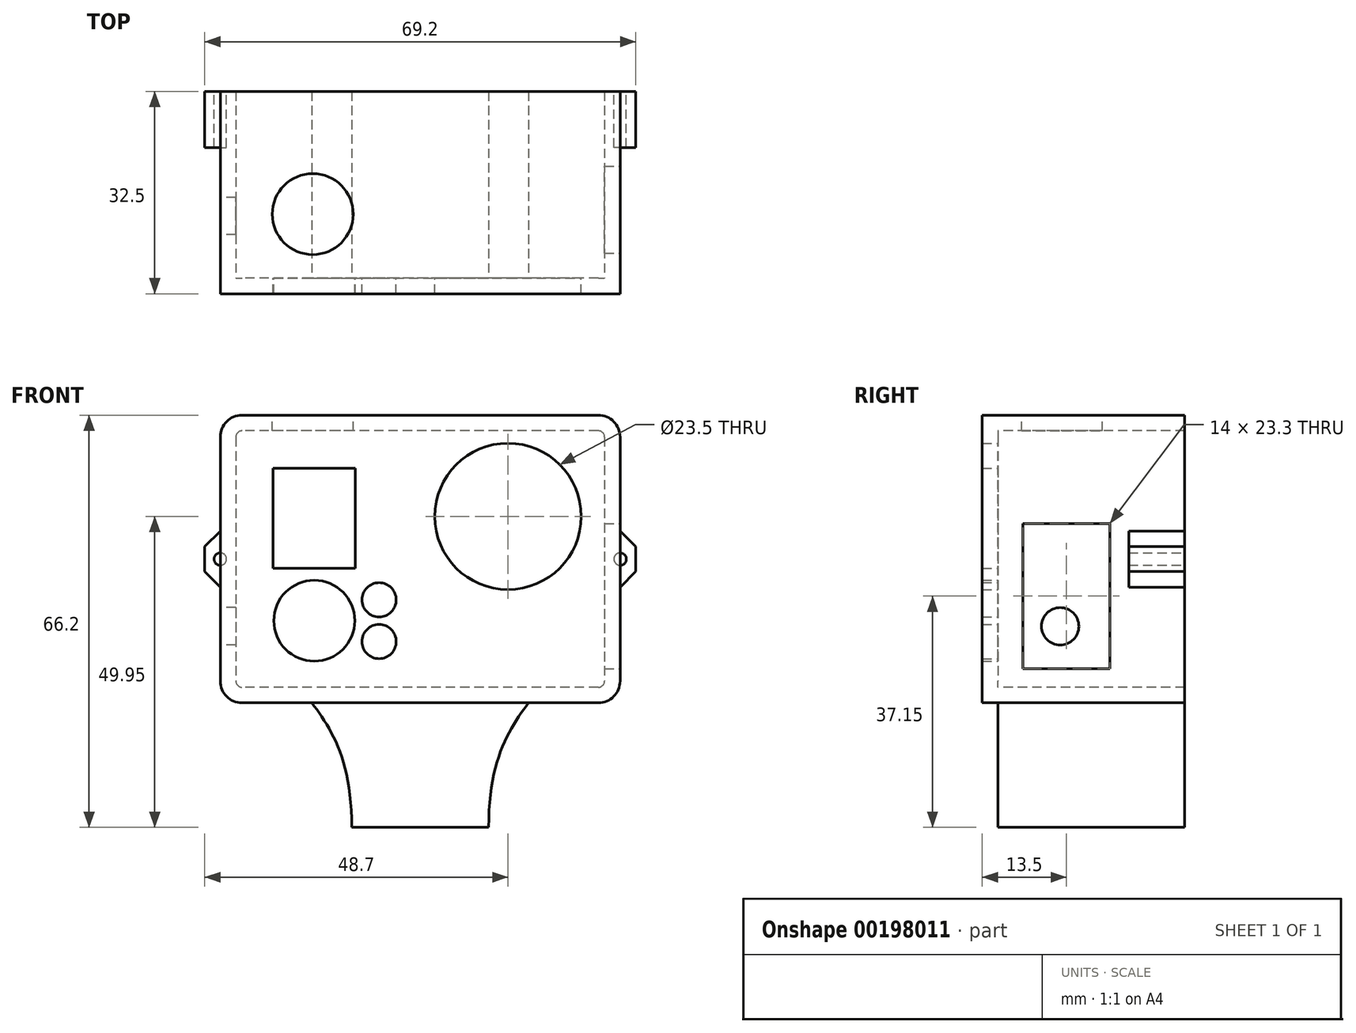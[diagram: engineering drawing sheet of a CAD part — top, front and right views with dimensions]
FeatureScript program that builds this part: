
annotation { "Feature Type Name" : "Feature", "Feature Type Description" : "" }
export const myFeature = defineFeature(function(context is Context, id is Id, definition is map)
    precondition{}
    {
        {
            var Q0;
            Q0=qCreatedBy(makeId("Front.planeOp"),FACE);
            var sketch = newSketch(context, id + "F0", { "sketchPlane" : qUnion([Q0])});
            skLineSegment(sketch, "E0.bottom", {"start": v(28.6, 20.6) * mm, "end": v(-28.6, 20.6) * mm});
            skLineSegment(sketch, "E0.top", {"start": v(28.6, -20.6) * mm, "end": v(-28.6, -20.6) * mm});
            skLineSegment(sketch, "E0.left", {"start": v(29.6, 19.6) * mm, "end": v(29.6, -19.6) * mm});
            skLineSegment(sketch, "E0.right", {"start": v(-29.6, 19.6) * mm, "end": v(-29.6, -19.6) * mm});
            skPoint(sketch, "E0.middle", {"position": v(0, 0) * mm});
            skCircle(sketch, "E1", {"center": v(14.1, 6.85) * mm, "radius": 11.75 * mm});
            skLineSegment(sketch, "E2.bottom", {"start": v(-23.6, 14.6) * mm, "end": v(-10.4, 14.6) * mm});
            skLineSegment(sketch, "E2.top", {"start": v(-23.6, -1.5) * mm, "end": v(-10.4, -1.5) * mm});
            skLineSegment(sketch, "E2.left", {"start": v(-23.6, 14.6) * mm, "end": v(-23.6, -1.5) * mm});
            skLineSegment(sketch, "E2.right", {"start": v(-10.4, 14.6) * mm, "end": v(-10.4, -1.5) * mm});
            skCircle(sketch, "E3", {"center": v(-17, -9.9) * mm, "radius": 6.5 * mm});
            skPoint(sketch, "E4", {"position": v(-17, -1.5) * mm});
            skCircle(sketch, "E5", {"center": v(-6.6, -13.25) * mm, "radius": 2.75 * mm});
            skLineSegment(sketch, "E6", {"start": v(-17, -9.9) * mm, "end": v(4.32, -9.9) * mm, "construction": true});
            skCircle(sketch, "E7.MirrorC", {"center": v(-6.6, -6.55) * mm, "radius": 2.75 * mm});
            skPoint(sketch, "E8.visualSharp", {"position": v(-29.6, 20.6) * mm});
            skArc(sketch, "E8.filletArc", {"start": v(-28.6, 20.6) * mm, "mid": v(-29.3, 20.3) * mm, "end": v(-29.6, 19.6) * mm});
            skPoint(sketch, "E9.visualSharp", {"position": v(-29.6, -20.6) * mm});
            skArc(sketch, "E9.filletArc", {"start": v(-29.6, -19.6) * mm, "mid": v(-29.3, -20.3) * mm, "end": v(-28.6, -20.6) * mm});
            skPoint(sketch, "E10.visualSharp", {"position": v(29.6, -20.6) * mm});
            skArc(sketch, "E10.filletArc", {"start": v(28.6, -20.6) * mm, "mid": v(29.3, -20.3) * mm, "end": v(29.6, -19.6) * mm});
            skPoint(sketch, "E11.visualSharp", {"position": v(29.6, 20.6) * mm});
            skArc(sketch, "E11.filletArc", {"start": v(29.6, 19.6) * mm, "mid": v(29.3, 20.3) * mm, "end": v(28.6, 20.6) * mm});
            skArc(sketch, "E12.0", {"start": v(32.1, 19.6) * mm, "mid": v(31.07, 22.07) * mm, "end": v(28.6, 23.1) * mm});
            skLineSegment(sketch, "E12.1", {"start": v(32.1, 19.6) * mm, "end": v(32.1, -19.6) * mm});
            skLineSegment(sketch, "E12.2", {"start": v(28.6, 23.1) * mm, "end": v(-28.6, 23.1) * mm});
            skArc(sketch, "E12.3", {"start": v(28.6, -23.1) * mm, "mid": v(31.07, -22.07) * mm, "end": v(32.1, -19.6) * mm});
            skArc(sketch, "E12.4", {"start": v(-28.6, 23.1) * mm, "mid": v(-31.07, 22.07) * mm, "end": v(-32.1, 19.6) * mm});
            skLineSegment(sketch, "E12.5", {"start": v(-32.1, 19.6) * mm, "end": v(-32.1, -19.6) * mm});
            skArc(sketch, "E12.6", {"start": v(-32.1, -19.6) * mm, "mid": v(-31.07, -22.07) * mm, "end": v(-28.6, -23.1) * mm});
            skLineSegment(sketch, "E12.7", {"start": v(28.6, -23.1) * mm, "end": v(-28.6, -23.1) * mm});
            skLineSegment(sketch, "E13", {"start": v(-11, -43.1) * mm, "end": v(11, -43.1) * mm});
            skPoint(sketch, "E14", {"position": v(0, -23.1) * mm});
            skPoint(sketch, "E15", {"position": v(0, -43.1) * mm});
            skLineSegment(sketch, "E16", {"start": v(-22.15, -12.1) * mm, "end": v(22.15, -12.1) * mm, "construction": true});
            skPoint(sketch, "E17", {"position": v(0, -12.1) * mm});
            skFitSpline(sketch, "E18", {"points": [v(22.15, -12.1) * mm, v(11, -43.1) * mm], "startDerivative": vector(0, -33) * mm, "endDerivative": vector(0, -60) * mm});
            skFitSpline(sketch, "E19", {"points": [v(-22.15, -12.1) * mm, v(-11, -43.1) * mm], "startDerivative": vector(0, -33) * mm, "endDerivative": vector(0, -60) * mm});
            skLineSegment(sketch, "E20", {"start": v(-24.4, -45.93) * mm, "end": v(17.2, -45.93) * mm, "construction": true});
            skSolve(sketch);
        }
        {
            var Q0;
            Q0=makeQuery(id+"F0.imprint","IMPRINT",FACE,{"disambiguationData":[TD([[makeQuery(id+"F0.imprint","IMPRINT",EDGE,{"derivedFrom":sQuery(id+"F0.wireOp",EDGE,"E0.bottom")}),-1.0]])]});
            var Q1;
            {var subQ0=sQuery(id+"F0.wireOp",EDGE,"E18");var subQ1=sQuery(id+"F0.wireOp",EDGE,"E0.top");var subQ2=makeQuery(id+"F0.imprint","INTERSECT",VERTEX,{"derivedFrom":[subQ1,subQ0]});Q1=makeQuery(id+"F0.imprint","IMPRINT",FACE,{"disambiguationData":[TD([[makeQuery(id+"F0.imprint","IMPRINT",EDGE,{"disambiguationData":[TD([[subQ2,-1.0]])],"derivedFrom":subQ1}),1.0]])]});}
            var Q2;
            {var subQ5=sQuery(id+"F0.wireOp",EDGE,"E13");Q2=makeQuery(id+"F0.imprint","IMPRINT",FACE,{"disambiguationData":[TD([[makeQuery(id+"F0.imprint","IMPRINT",EDGE,{"derivedFrom":subQ5}),1.0]])]});}
            extrude(context, id + "F1", {"entities" : qUnion([Q0, Q1, Q2]), "oppositeDirection" : true, "depth" : 30 * mm});
        }
        {
            var Q0;
            Q0=makeQuery(id+"F0.imprint","IMPRINT",FACE,{"disambiguationData":[TD([[makeQuery(id+"F0.imprint","IMPRINT",EDGE,{"derivedFrom":sQuery(id+"F0.wireOp",EDGE,"E0.bottom")}),-1.0]])]});
            var Q1;
            Q1=makeQuery(id+"F0.imprint","IMPRINT",FACE,{"disambiguationData":[TD([[makeQuery(id+"F0.imprint","IMPRINT",EDGE,{"derivedFrom":sQuery(id+"F0.wireOp",EDGE,"E0.bottom")}),1.0]])]});
            var Q2;
            {var subQ0=sQuery(id+"F0.wireOp",EDGE,"E18");var subQ1=sQuery(id+"F0.wireOp",EDGE,"E0.top");var subQ2=makeQuery(id+"F0.imprint","INTERSECT",VERTEX,{"derivedFrom":[subQ1,subQ0]});Q2=makeQuery(id+"F0.imprint","IMPRINT",FACE,{"disambiguationData":[TD([[makeQuery(id+"F0.imprint","IMPRINT",EDGE,{"disambiguationData":[TD([[subQ2,-1.0]])],"derivedFrom":subQ1}),1.0]])]});}
            extrude(context, id + "F2", {"entities" : qUnion([Q0, Q1, Q2]), "operationType" : NewBodyOperationType.ADD, "depth" : 2.5 * mm});
        }
        {
            var Q0;
            {var subQ0=sQuery(id+"F0.wireOp",EDGE,"E12.2");Q0=makeQuery(id+"F2.boolean.opBoolean","MERGE",FACE,{"derivedFrom":[makeQuery(id+"F1.opExtrude","SWEPT_FACE",FACE,{"disambiguationData":[OSD([subQ0])]}),makeQuery(id+"F2.opExtrude","SWEPT_FACE",FACE,{"disambiguationData":[OSD([subQ0])]})]});}
            var sketch = newSketch(context, id + "F3", { "sketchPlane" : qUnion([Q0])});
            skCircle(sketch, "E21", {"center": v(-17.25, 10.3) * mm, "radius": 6.5 * mm});
            skSolve(sketch);
        }
        {
            var Q0;
            Q0=makeQuery(id+"F3.imprint","IMPRINT",FACE,{"disambiguationData":[TD([[makeQuery(id+"F3.imprint","IMPRINT",EDGE,{"derivedFrom":sQuery(id+"F3.wireOp",EDGE,"E21")}),1.0]])]});
            extrude(context, id + "F4", {"entities" : qUnion([Q0]), "operationType" : NewBodyOperationType.REMOVE, "endBound" : BoundingType.UP_TO_NEXT, "oppositeDirection" : true, "depth" : 25 * mm});
        }
        {
            var Q0;
            {var subQ0=sQuery(id+"F0.wireOp",EDGE,"E12.5");Q0=makeQuery(id+"F2.boolean.opBoolean","MERGE",FACE,{"derivedFrom":[makeQuery(id+"F1.opExtrude","SWEPT_FACE",FACE,{"disambiguationData":[OSD([subQ0])]}),makeQuery(id+"F2.opExtrude","SWEPT_FACE",FACE,{"disambiguationData":[OSD([subQ0])]})]});}
            var sketch = newSketch(context, id + "F5", { "sketchPlane" : qUnion([Q0])});
            skCircle(sketch, "E22", {"center": v(-10, -10.8) * mm, "radius": 3 * mm});
            skLineSegment(sketch, "E23.bottom", {"start": v(-30, 4.5) * mm, "end": v(-21, 4.5) * mm});
            skLineSegment(sketch, "E23.top", {"start": v(-30, -4.5) * mm, "end": v(-21, -4.5) * mm});
            skLineSegment(sketch, "E23.left", {"start": v(-30, 4.5) * mm, "end": v(-30, -4.5) * mm});
            skLineSegment(sketch, "E23.right", {"start": v(-21, 4.5) * mm, "end": v(-21, -4.5) * mm});
            skPoint(sketch, "E24", {"position": v(-30, 0) * mm});
            skSolve(sketch);
        }
        {
            var Q0;
            Q0=makeQuery(id+"F5.imprint","IMPRINT",FACE,{"disambiguationData":[TD([[makeQuery(id+"F5.imprint","IMPRINT",EDGE,{"derivedFrom":sQuery(id+"F5.wireOp",EDGE,"E22")}),1.0]])]});
            extrude(context, id + "F6", {"entities" : qUnion([Q0]), "operationType" : NewBodyOperationType.REMOVE, "endBound" : BoundingType.UP_TO_NEXT, "oppositeDirection" : true, "depth" : 25 * mm});
        }
        {
            var Q0;
            {var subQ0=sQuery(id+"F0.wireOp",EDGE,"E12.1");Q0=makeQuery(id+"F2.boolean.opBoolean","MERGE",FACE,{"derivedFrom":[makeQuery(id+"F1.opExtrude","SWEPT_FACE",FACE,{"disambiguationData":[OSD([subQ0])]}),makeQuery(id+"F2.opExtrude","SWEPT_FACE",FACE,{"disambiguationData":[OSD([subQ0])]})]});}
            var sketch = newSketch(context, id + "F7", { "sketchPlane" : qUnion([Q0])});
            skLineSegment(sketch, "E25.bottom", {"start": v(4, 5.7) * mm, "end": v(18, 5.7) * mm});
            skLineSegment(sketch, "E25.top", {"start": v(4, -17.6) * mm, "end": v(18, -17.6) * mm});
            skLineSegment(sketch, "E25.left", {"start": v(4, 5.7) * mm, "end": v(4, -17.6) * mm});
            skLineSegment(sketch, "E25.right", {"start": v(18, 5.7) * mm, "end": v(18, -17.6) * mm});
            skLineSegment(sketch, "E26.bottom", {"start": v(21, 4.5) * mm, "end": v(30, 4.5) * mm});
            skLineSegment(sketch, "E26.top", {"start": v(21, -4.5) * mm, "end": v(30, -4.5) * mm});
            skLineSegment(sketch, "E26.left", {"start": v(21, 4.5) * mm, "end": v(21, -4.5) * mm});
            skLineSegment(sketch, "E26.right", {"start": v(30, 4.5) * mm, "end": v(30, -4.5) * mm});
            skPoint(sketch, "E27", {"position": v(30, 0) * mm});
            skSolve(sketch);
        }
        {
            var Q0;
            Q0=makeQuery(id+"F7.imprint","IMPRINT",FACE,{"disambiguationData":[TD([[makeQuery(id+"F7.imprint","IMPRINT",EDGE,{"derivedFrom":sQuery(id+"F7.wireOp",EDGE,"E25.bottom")}),-1.0]])]});
            extrude(context, id + "F8", {"entities" : qUnion([Q0]), "operationType" : NewBodyOperationType.REMOVE, "endBound" : BoundingType.UP_TO_NEXT, "oppositeDirection" : true, "depth" : 25 * mm});
        }
        {
            var Q0;
            Q0=makeQuery(id+"F5.imprint","IMPRINT",FACE,{"disambiguationData":[TD([[makeQuery(id+"F5.imprint","IMPRINT",EDGE,{"derivedFrom":sQuery(id+"F5.wireOp",EDGE,"E23.bottom")}),-1.0]])]});
            extrude(context, id + "F9", {"entities" : qUnion([Q0]), "operationType" : NewBodyOperationType.ADD, "depth" : 2.5 * mm});
        }
        {
            var Q0;
            Q0=makeQuery(id+"F7.imprint","IMPRINT",FACE,{"disambiguationData":[TD([[makeQuery(id+"F7.imprint","IMPRINT",EDGE,{"derivedFrom":sQuery(id+"F7.wireOp",EDGE,"E26.bottom")}),-1.0]])]});
            extrude(context, id + "F10", {"entities" : qUnion([Q0]), "operationType" : NewBodyOperationType.ADD, "depth" : 2.5 * mm});
        }
        {
            var Q0;
            Q0=makeQuery(id+"F9.opExtrude","CAP_EDGE",EDGE,{"disambiguationData":[OSD([sQuery(id+"F5.wireOp",EDGE,"E23.top")])],"isStart":false});
            var Q1;
            Q1=makeQuery(id+"F9.opExtrude","CAP_EDGE",EDGE,{"disambiguationData":[OSD([sQuery(id+"F5.wireOp",EDGE,"E23.bottom")])],"isStart":false});
            var Q2;
            Q2=makeQuery(id+"F10.opExtrude","CAP_EDGE",EDGE,{"disambiguationData":[OSD([sQuery(id+"F7.wireOp",EDGE,"E26.bottom")])],"isStart":false});
            var Q3;
            Q3=makeQuery(id+"F10.opExtrude","CAP_EDGE",EDGE,{"disambiguationData":[OSD([sQuery(id+"F7.wireOp",EDGE,"E26.top")])],"isStart":false});
            chamfer(context, id + "F11", {"entities" : qUnion([Q0, Q1, Q2, Q3]), "width" : 2.5 * mm, "tangentPropagation" : true});
        }
        {
            var Q0;
            Q0=makeQuery(id+"F10.boolean.opBoolean","MERGE",FACE,{"derivedFrom":[makeQuery(id+"F9.boolean.opBoolean","MERGE",FACE,{"derivedFrom":[makeQuery(id+"F1.opExtrude","CAP_FACE",FACE,{"disambiguationData":[OSD([sQuery(id+"F0.wireOp",EDGE,"E0.bottom"),sQuery(id+"F0.wireOp",EDGE,"E0.top"),sQuery(id+"F0.wireOp",EDGE,"E0.left"),sQuery(id+"F0.wireOp",EDGE,"E0.right"),sQuery(id+"F0.wireOp",EDGE,"E8.filletArc"),sQuery(id+"F0.wireOp",EDGE,"E9.filletArc"),sQuery(id+"F0.wireOp",EDGE,"E10.filletArc"),sQuery(id+"F0.wireOp",EDGE,"E11.filletArc"),sQuery(id+"F0.wireOp",EDGE,"E12.0"),sQuery(id+"F0.wireOp",EDGE,"E12.1"),sQuery(id+"F0.wireOp",EDGE,"E12.2"),sQuery(id+"F0.wireOp",EDGE,"E12.3"),sQuery(id+"F0.wireOp",EDGE,"E12.4"),sQuery(id+"F0.wireOp",EDGE,"E12.5"),sQuery(id+"F0.wireOp",EDGE,"E12.6"),sQuery(id+"F0.wireOp",EDGE,"E12.7")])],"isStart":false}),makeQuery(id+"F9.opExtrude","SWEPT_FACE",FACE,{"disambiguationData":[OSD([sQuery(id+"F5.wireOp",EDGE,"E23.left")])]})]}),makeQuery(id+"F10.opExtrude","SWEPT_FACE",FACE,{"disambiguationData":[OSD([sQuery(id+"F7.wireOp",EDGE,"E26.right")])]})]});
            var sketch = newSketch(context, id + "F12", { "sketchPlane" : qUnion([Q0])});
            skPoint(sketch, "E28", {"position": v(32.1, 0) * mm});
            skPoint(sketch, "E29", {"position": v(-32.1, 0) * mm});
            skCircle(sketch, "E30", {"center": v(32.1, 0) * mm, "radius": 1 * mm});
            skCircle(sketch, "E31", {"center": v(-32.1, 0) * mm, "radius": 1 * mm});
            skSolve(sketch);
        }
        {
            var Q0;
            Q0=makeQuery(id+"F12.imprint","IMPRINT",FACE,{"disambiguationData":[TD([[makeQuery(id+"F12.imprint","IMPRINT",EDGE,{"derivedFrom":sQuery(id+"F12.wireOp",EDGE,"E31")}),1.0]])]});
            var Q1;
            Q1=makeQuery(id+"F12.imprint","IMPRINT",FACE,{"disambiguationData":[TD([[makeQuery(id+"F12.imprint","IMPRINT",EDGE,{"derivedFrom":sQuery(id+"F12.wireOp",EDGE,"E30")}),1.0]])]});
            var Q2;
            Q2=sQuery(id+"F12.wireOp",EDGE,"E31");
            var Q3;
            Q3=sQuery(id+"F12.wireOp",EDGE,"E30");
            extrude(context, id + "F13", {"entities" : qUnion([Q0, Q1]), "operationType" : NewBodyOperationType.REMOVE, "surfaceEntities" : qUnion([Q2, Q3]), "oppositeDirection" : true, "depth" : 9 * mm});
        }
        {
            var Q0;
            Q0=sQuery(id+"F0.wireOp",EDGE,"E20");
            var Q1;
            {var subQ5=sQuery(id+"F0.wireOp",EDGE,"E13");Q1=makeQuery(id+"F0.imprint","IMPRINT",FACE,{"disambiguationData":[TD([[makeQuery(id+"F0.imprint","IMPRINT",EDGE,{"derivedFrom":subQ5}),1.0]])]});}
            cPlane(context, id + "F14", {"entities" : qUnion([Q0, Q1]), "cplaneType" : CPlaneType.LINE_ANGLE, "offset" : 25 * mm, "angle" : 25 * degree, "width" : 150 * mm, "height" : 150 * mm});
        }
    });
